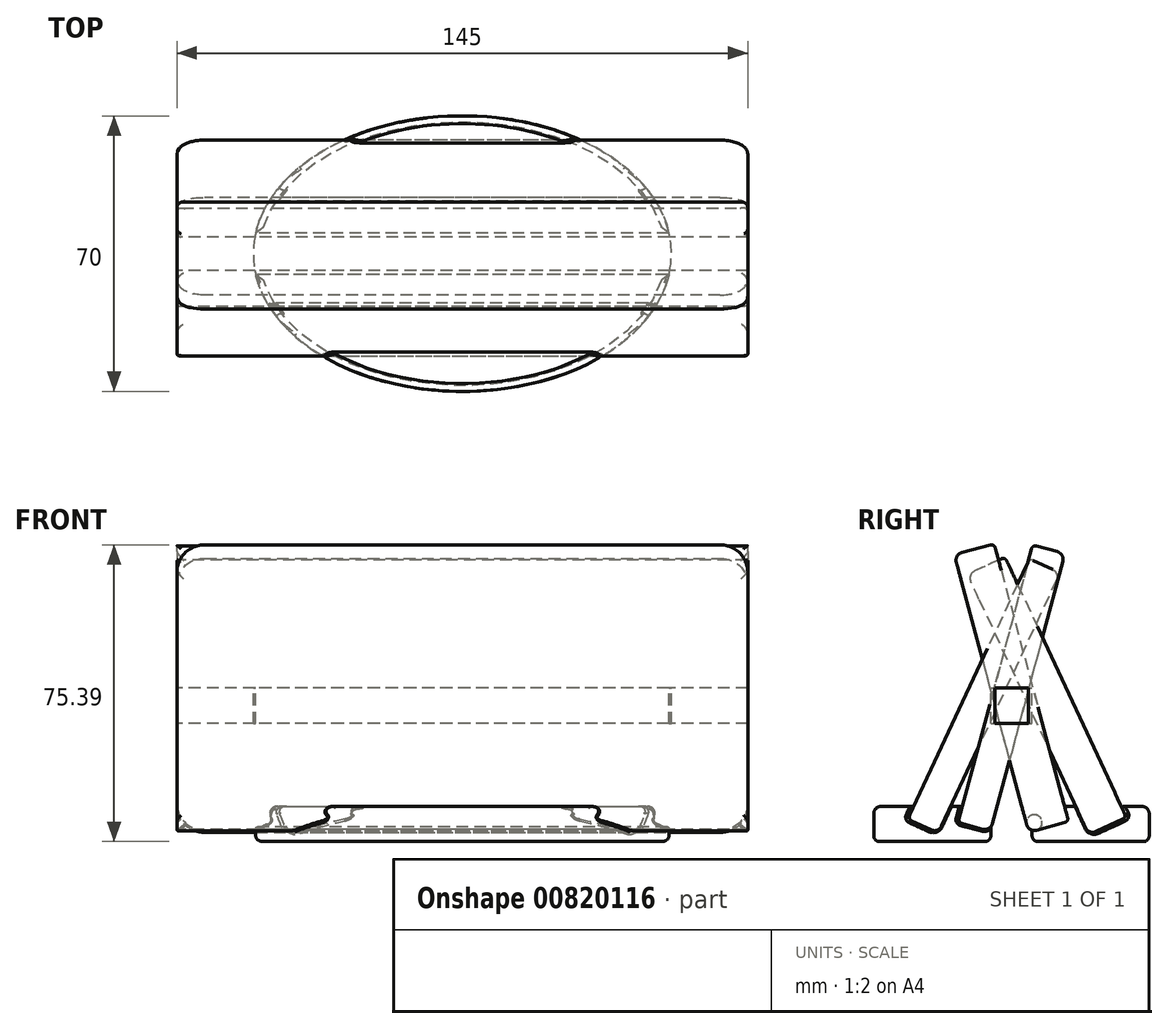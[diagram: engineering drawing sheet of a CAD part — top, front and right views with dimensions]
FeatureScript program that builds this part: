
annotation { "Feature Type Name" : "Feature", "Feature Type Description" : "" }
export const myFeature = defineFeature(function(context is Context, id is Id, definition is map)
    precondition{}
    {
        {
            var Q0;
            Q0=qCreatedBy(makeId("Top.planeOp"),FACE);
            var sketch = newSketch(context, id + "F0", { "sketchPlane" : qUnion([Q0])});
            skLineSegment(sketch, "E0.bottom", {"start": v(72.5, 5.25) * mm, "end": v(-72.5, 5.25) * mm});
            skLineSegment(sketch, "E0.top", {"start": v(72.5, -5.25) * mm, "end": v(-72.5, -5.25) * mm});
            skLineSegment(sketch, "E0.left", {"start": v(72.5, 5.25) * mm, "end": v(72.5, -5.25) * mm});
            skLineSegment(sketch, "E0.right", {"start": v(-72.5, 5.25) * mm, "end": v(-72.5, -5.25) * mm});
            skPoint(sketch, "E0.middle", {"position": v(0, 0) * mm});
            skLineSegment(sketch, "E1", {"start": v(-72.5, 0) * mm, "end": v(72.5, 0) * mm, "construction": true});
            skLineSegment(sketch, "E2", {"start": v(52.5, 5.25) * mm, "end": v(52.5, -5.25) * mm, "construction": true});
            skLineSegment(sketch, "E3", {"start": v(0, 0) * mm, "end": v(0, 35) * mm, "construction": true});
            skEllipse(sketch, "E4", {"center": v(0, 0) * mm, "majorRadius": 53.1 * mm, "minorRadius": 35 * mm, "majorAxis": v(1, 0)});
            skLineSegment(sketch, "E5", {"start": v(0, 35) * mm, "end": v(0, 40) * mm, "construction": true});
            skFitSpline(sketch, "E6.0", {"points": [v(58.05, -2.11) * mm, v(58.13, 0) * mm, v(58.05, 2.11) * mm, v(57.73, 4.9) * mm, v(56.95, 8.34) * mm, v(55.44, 12.3) * mm, v(53.38, 16.09) * mm, v(50.8, 19.67) * mm, v(47.77, 23.01) * mm, v(44.86, 25.6) * mm, v(42.32, 27.54) * mm, v(40.31, 28.94) * mm, v(38.21, 30.25) * mm, v(35.32, 31.9) * mm, v(31.51, 33.75) * mm, v(26.7, 35.65) * mm, v(21.67, 37.22) * mm, v(16.45, 38.45) * mm, v(11.08, 39.34) * mm, v(6.5, 39.79) * mm, v(2.8, 39.97) * mm, v(0, 40.02) * mm, v(-2.8, 39.97) * mm, v(-6.5, 39.79) * mm, v(-11.08, 39.34) * mm, v(-16.45, 38.45) * mm, v(-21.67, 37.22) * mm, v(-26.7, 35.65) * mm, v(-31.51, 33.75) * mm, v(-35.32, 31.9) * mm, v(-38.21, 30.25) * mm, v(-40.31, 28.94) * mm, v(-42.32, 27.54) * mm, v(-44.86, 25.6) * mm, v(-47.77, 23.01) * mm, v(-50.8, 19.67) * mm, v(-53.38, 16.09) * mm, v(-55.44, 12.3) * mm, v(-56.95, 8.34) * mm, v(-57.73, 4.9) * mm, v(-58.05, 2.11) * mm, v(-58.13, 0) * mm, v(-58.05, -2.11) * mm, v(-57.73, -4.9) * mm, v(-56.95, -8.34) * mm, v(-55.44, -12.3) * mm, v(-53.38, -16.09) * mm, v(-50.8, -19.67) * mm, v(-47.77, -23.01) * mm, v(-44.86, -25.6) * mm, v(-42.32, -27.54) * mm, v(-40.31, -28.94) * mm, v(-38.21, -30.25) * mm, v(-35.32, -31.9) * mm, v(-31.51, -33.75) * mm, v(-26.7, -35.65) * mm, v(-21.67, -37.22) * mm, v(-16.45, -38.45) * mm, v(-11.08, -39.34) * mm, v(-6.5, -39.79) * mm, v(-2.8, -39.97) * mm, v(0, -40.02) * mm, v(2.8, -39.97) * mm, v(6.5, -39.79) * mm, v(11.08, -39.34) * mm, v(16.45, -38.45) * mm, v(21.67, -37.22) * mm, v(26.7, -35.65) * mm, v(31.51, -33.75) * mm, v(35.32, -31.9) * mm, v(38.21, -30.25) * mm, v(40.31, -28.94) * mm, v(42.32, -27.54) * mm, v(44.86, -25.6) * mm, v(47.77, -23.01) * mm, v(50.8, -19.67) * mm, v(53.38, -16.09) * mm, v(55.44, -12.3) * mm, v(56.95, -8.34) * mm, v(57.73, -4.9) * mm, v(58.05, -2.11) * mm, v(58.13, 0) * mm, v(58.05, 2.11) * mm, v(58.05, -2.11) * mm]});
            skLineSegment(sketch, "E7.bottom", {"start": v(72.5, -4.25) * mm, "end": v(-72.5, -4.25) * mm});
            skLineSegment(sketch, "E7.top", {"start": v(72.5, 4.25) * mm, "end": v(-72.5, 4.25) * mm});
            skLineSegment(sketch, "E7.left", {"start": v(72.5, -4.25) * mm, "end": v(72.5, 4.25) * mm});
            skLineSegment(sketch, "E7.right", {"start": v(-72.5, -4.25) * mm, "end": v(-72.5, 4.25) * mm});
            skSolve(sketch);
        }
        {
            var Q0;
            {var subQ5=sQuery(id+"F0.wireOp",EDGE,"E7.right");Q0=makeQuery(id+"F0.imprint","IMPRINT",FACE,{"disambiguationData":[TD([[makeQuery(id+"F0.imprint","IMPRINT",EDGE,{"derivedFrom":subQ5}),-1.0]])]});}
            var Q1;
            {var subQ0=sQuery(id+"F0.wireOp",EDGE,"E7.top");var subQ1=sQuery(id+"F0.wireOp",EDGE,"E4");var subQ2=makeQuery(id+"F0.imprint","INTERSECT",VERTEX,{"disambiguationData":[OD(1.0)],"derivedFrom":[subQ1,subQ0]});Q1=makeQuery(id+"F0.imprint","IMPRINT",FACE,{"disambiguationData":[TD([[makeQuery(id+"F0.imprint","IMPRINT",EDGE,{"disambiguationData":[TD([[subQ2,-1.0]])],"derivedFrom":subQ1}),-1.0]])]});}
            var Q2;
            {var subQ0=sQuery(id+"F0.wireOp",EDGE,"E7.top");var subQ1=sQuery(id+"F0.wireOp",EDGE,"E4");var subQ2=makeQuery(id+"F0.imprint","INTERSECT",VERTEX,{"disambiguationData":[OD(1.0)],"derivedFrom":[subQ1,subQ0]});Q2=makeQuery(id+"F0.imprint","IMPRINT",FACE,{"disambiguationData":[TD([[makeQuery(id+"F0.imprint","IMPRINT",EDGE,{"disambiguationData":[TD([[subQ2,-1.0]])],"derivedFrom":subQ1}),1.0]])]});}
            var Q3;
            {var subQ0=sQuery(id+"F0.wireOp",EDGE,"E7.top");var subQ1=sQuery(id+"F0.wireOp",EDGE,"E4");var subQ2=makeQuery(id+"F0.imprint","INTERSECT",VERTEX,{"disambiguationData":[OD(0.0)],"derivedFrom":[subQ1,subQ0]});Q3=makeQuery(id+"F0.imprint","IMPRINT",FACE,{"disambiguationData":[TD([[makeQuery(id+"F0.imprint","IMPRINT",EDGE,{"disambiguationData":[TD([[subQ2,1.0]])],"derivedFrom":subQ1}),-1.0]])]});}
            var Q4;
            {var subQ5=sQuery(id+"F0.wireOp",EDGE,"E7.left");Q4=makeQuery(id+"F0.imprint","IMPRINT",FACE,{"disambiguationData":[TD([[makeQuery(id+"F0.imprint","IMPRINT",EDGE,{"derivedFrom":subQ5}),1.0]])]});}
            extrude(context, id + "F1", {"entities" : qUnion([Q0, Q1, Q2, Q3, Q4]), "depth" : 73 * mm, "offsetDistance" : 25 * mm, "symmetric" : true});
        }
        {
            var Q0;
            {var subQ5=sQuery(id+"F0.wireOp",EDGE,"E7.left");Q0=makeQuery(id+"F0.imprint","IMPRINT",FACE,{"disambiguationData":[TD([[makeQuery(id+"F0.imprint","IMPRINT",EDGE,{"derivedFrom":subQ5}),1.0]])]});}
            var Q1;
            {var subQ0=sQuery(id+"F0.wireOp",EDGE,"E0.left");var subQ1=sQuery(id+"F0.wireOp",EDGE,"E0.bottom");var subQ2=makeQuery(id+"F0.imprint","INTERSECT",VERTEX,{"derivedFrom":[subQ1,subQ0]});Q1=makeQuery(id+"F0.imprint","IMPRINT",FACE,{"disambiguationData":[TD([[makeQuery(id+"F0.imprint","IMPRINT",EDGE,{"disambiguationData":[TD([[subQ2,-1.0]])],"derivedFrom":subQ1}),1.0]])]});}
            var Q2;
            {var subQ0=sQuery(id+"F0.wireOp",EDGE,"E0.left");var subQ1=sQuery(id+"F0.wireOp",EDGE,"E0.top");var subQ2=makeQuery(id+"F0.imprint","INTERSECT",VERTEX,{"derivedFrom":[subQ1,subQ0]});Q2=makeQuery(id+"F0.imprint","IMPRINT",FACE,{"disambiguationData":[TD([[makeQuery(id+"F0.imprint","IMPRINT",EDGE,{"disambiguationData":[TD([[subQ2,-1.0]])],"derivedFrom":subQ1}),-1.0]])]});}
            var Q3;
            {var subQ0=sQuery(id+"F0.wireOp",EDGE,"E7.top");var subQ1=sQuery(id+"F0.wireOp",EDGE,"E4");var subQ2=makeQuery(id+"F0.imprint","INTERSECT",VERTEX,{"disambiguationData":[OD(0.0)],"derivedFrom":[subQ1,subQ0]});Q3=makeQuery(id+"F0.imprint","IMPRINT",FACE,{"disambiguationData":[TD([[makeQuery(id+"F0.imprint","IMPRINT",EDGE,{"disambiguationData":[TD([[subQ2,1.0]])],"derivedFrom":subQ1}),-1.0]])]});}
            var Q4;
            {var subQ0=sQuery(id+"F0.wireOp",EDGE,"E6.0");var subQ1=sQuery(id+"F0.wireOp",EDGE,"E0.bottom");var subQ2=makeQuery(id+"F0.imprint","INTERSECT",VERTEX,{"disambiguationData":[OD(0.0)],"derivedFrom":[subQ1,subQ0]});Q4=makeQuery(id+"F0.imprint","IMPRINT",FACE,{"disambiguationData":[TD([[makeQuery(id+"F0.imprint","IMPRINT",EDGE,{"disambiguationData":[TD([[subQ2,-1.0]])],"derivedFrom":subQ1}),1.0]])]});}
            var Q5;
            {var subQ0=sQuery(id+"F0.wireOp",EDGE,"E6.0");var subQ1=sQuery(id+"F0.wireOp",EDGE,"E0.top");var subQ2=makeQuery(id+"F0.imprint","INTERSECT",VERTEX,{"disambiguationData":[OD(0.0)],"derivedFrom":[subQ1,subQ0]});Q5=makeQuery(id+"F0.imprint","IMPRINT",FACE,{"disambiguationData":[TD([[makeQuery(id+"F0.imprint","IMPRINT",EDGE,{"disambiguationData":[TD([[subQ2,-1.0]])],"derivedFrom":subQ1}),-1.0]])]});}
            var Q6;
            {var subQ0=sQuery(id+"F0.wireOp",EDGE,"E7.top");var subQ1=sQuery(id+"F0.wireOp",EDGE,"E4");var subQ2=makeQuery(id+"F0.imprint","INTERSECT",VERTEX,{"disambiguationData":[OD(1.0)],"derivedFrom":[subQ1,subQ0]});Q6=makeQuery(id+"F0.imprint","IMPRINT",FACE,{"disambiguationData":[TD([[makeQuery(id+"F0.imprint","IMPRINT",EDGE,{"disambiguationData":[TD([[subQ2,-1.0]])],"derivedFrom":subQ1}),1.0]])]});}
            var Q7;
            {var subQ0=sQuery(id+"F0.wireOp",EDGE,"E4");var subQ1=sQuery(id+"F0.wireOp",EDGE,"E0.bottom");var subQ2=makeQuery(id+"F0.imprint","INTERSECT",VERTEX,{"disambiguationData":[OD(0.0)],"derivedFrom":[subQ1,subQ0]});Q7=makeQuery(id+"F0.imprint","IMPRINT",FACE,{"disambiguationData":[TD([[makeQuery(id+"F0.imprint","IMPRINT",EDGE,{"disambiguationData":[TD([[subQ2,-1.0]])],"derivedFrom":subQ1}),1.0]])]});}
            var Q8;
            {var subQ0=sQuery(id+"F0.wireOp",EDGE,"E4");var subQ1=sQuery(id+"F0.wireOp",EDGE,"E0.top");var subQ2=makeQuery(id+"F0.imprint","INTERSECT",VERTEX,{"disambiguationData":[OD(0.0)],"derivedFrom":[subQ1,subQ0]});Q8=makeQuery(id+"F0.imprint","IMPRINT",FACE,{"disambiguationData":[TD([[makeQuery(id+"F0.imprint","IMPRINT",EDGE,{"disambiguationData":[TD([[subQ2,-1.0]])],"derivedFrom":subQ1}),-1.0]])]});}
            var Q9;
            {var subQ0=sQuery(id+"F0.wireOp",EDGE,"E6.0");var subQ1=sQuery(id+"F0.wireOp",EDGE,"E0.bottom");var subQ2=makeQuery(id+"F0.imprint","INTERSECT",VERTEX,{"disambiguationData":[OD(1.0)],"derivedFrom":[subQ1,subQ0]});Q9=makeQuery(id+"F0.imprint","IMPRINT",FACE,{"disambiguationData":[TD([[makeQuery(id+"F0.imprint","IMPRINT",EDGE,{"disambiguationData":[TD([[subQ2,1.0]])],"derivedFrom":subQ1}),1.0]])]});}
            var Q10;
            {var subQ0=sQuery(id+"F0.wireOp",EDGE,"E7.top");var subQ1=sQuery(id+"F0.wireOp",EDGE,"E4");var subQ2=makeQuery(id+"F0.imprint","INTERSECT",VERTEX,{"disambiguationData":[OD(1.0)],"derivedFrom":[subQ1,subQ0]});Q10=makeQuery(id+"F0.imprint","IMPRINT",FACE,{"disambiguationData":[TD([[makeQuery(id+"F0.imprint","IMPRINT",EDGE,{"disambiguationData":[TD([[subQ2,-1.0]])],"derivedFrom":subQ1}),-1.0]])]});}
            var Q11;
            {var subQ0=sQuery(id+"F0.wireOp",EDGE,"E6.0");var subQ1=sQuery(id+"F0.wireOp",EDGE,"E0.top");var subQ2=makeQuery(id+"F0.imprint","INTERSECT",VERTEX,{"disambiguationData":[OD(1.0)],"derivedFrom":[subQ1,subQ0]});Q11=makeQuery(id+"F0.imprint","IMPRINT",FACE,{"disambiguationData":[TD([[makeQuery(id+"F0.imprint","IMPRINT",EDGE,{"disambiguationData":[TD([[subQ2,1.0]])],"derivedFrom":subQ1}),-1.0]])]});}
            var Q12;
            {var subQ0=sQuery(id+"F0.wireOp",EDGE,"E0.right");var subQ1=sQuery(id+"F0.wireOp",EDGE,"E0.bottom");var subQ2=makeQuery(id+"F0.imprint","INTERSECT",VERTEX,{"derivedFrom":[subQ1,subQ0]});Q12=makeQuery(id+"F0.imprint","IMPRINT",FACE,{"disambiguationData":[TD([[makeQuery(id+"F0.imprint","IMPRINT",EDGE,{"disambiguationData":[TD([[subQ2,1.0]])],"derivedFrom":subQ1}),1.0]])]});}
            var Q13;
            {var subQ5=sQuery(id+"F0.wireOp",EDGE,"E7.right");Q13=makeQuery(id+"F0.imprint","IMPRINT",FACE,{"disambiguationData":[TD([[makeQuery(id+"F0.imprint","IMPRINT",EDGE,{"derivedFrom":subQ5}),-1.0]])]});}
            var Q14;
            {var subQ0=sQuery(id+"F0.wireOp",EDGE,"E0.right");var subQ1=sQuery(id+"F0.wireOp",EDGE,"E0.top");var subQ2=makeQuery(id+"F0.imprint","INTERSECT",VERTEX,{"derivedFrom":[subQ1,subQ0]});Q14=makeQuery(id+"F0.imprint","IMPRINT",FACE,{"disambiguationData":[TD([[makeQuery(id+"F0.imprint","IMPRINT",EDGE,{"disambiguationData":[TD([[subQ2,1.0]])],"derivedFrom":subQ1}),-1.0]])]});}
            extrude(context, id + "F2", {"entities" : qUnion([Q0, Q1, Q2, Q3, Q4, Q5, Q6, Q7, Q8, Q9, Q10, Q11, Q12, Q13, Q14]), "depth" : 73 * mm, "offsetDistance" : 25 * mm, "symmetric" : true});
        }
        {
            var Q0;
            Q0=makeQuery(id+"F1.opExtrude","CAP_EDGE",EDGE,{"disambiguationData":[OSD([sQuery(id+"F0.wireOp",EDGE,"E7.left")])],"isStart":false});
            var Q1;
            Q1=makeQuery(id+"F1.opExtrude","CAP_EDGE",EDGE,{"disambiguationData":[OSD([sQuery(id+"F0.wireOp",EDGE,"E7.right")])],"isStart":false});
            var Q2;
            Q2=makeQuery(id+"F1.opExtrude","CAP_EDGE",EDGE,{"disambiguationData":[OSD([sQuery(id+"F0.wireOp",EDGE,"E7.left")])],"isStart":true});
            var Q3;
            Q3=makeQuery(id+"F1.opExtrude","CAP_EDGE",EDGE,{"disambiguationData":[OSD([sQuery(id+"F0.wireOp",EDGE,"E7.right")])],"isStart":true});
            var Q4;
            Q4=makeQuery(id+"F2.opExtrude","CAP_EDGE",EDGE,{"disambiguationData":[OSD([sQuery(id+"F0.wireOp",EDGE,"E0.right"),sQuery(id+"F0.wireOp",EDGE,"E7.right")])],"isStart":false});
            var Q5;
            Q5=makeQuery(id+"F2.opExtrude","CAP_EDGE",EDGE,{"disambiguationData":[OSD([sQuery(id+"F0.wireOp",EDGE,"E0.right"),sQuery(id+"F0.wireOp",EDGE,"E7.right")])],"isStart":true});
            var Q6;
            Q6=makeQuery(id+"F2.opExtrude","CAP_EDGE",EDGE,{"disambiguationData":[OSD([sQuery(id+"F0.wireOp",EDGE,"E0.left"),sQuery(id+"F0.wireOp",EDGE,"E7.left")])],"isStart":false});
            var Q7;
            Q7=makeQuery(id+"F2.opExtrude","CAP_EDGE",EDGE,{"disambiguationData":[OSD([sQuery(id+"F0.wireOp",EDGE,"E0.left"),sQuery(id+"F0.wireOp",EDGE,"E7.left")])],"isStart":true});
            fillet(context, id + "F3", {"entities" : qUnion([Q0, Q1, Q2, Q3, Q4, Q5, Q6, Q7]), "radius" : 7 * mm, "tangentPropagation" : true, "allowEdgeOverflow" : false});
        }
        {
            var Q0;
            Q0=makeQuery(id+"F1.opExtrude","SWEPT_BODY",BODY,{"disambiguationData":[OSD([sQuery(id+"F0.wireOp",EDGE,"E7.bottom"),sQuery(id+"F0.wireOp",EDGE,"E7.top"),sQuery(id+"F0.wireOp",EDGE,"E7.left"),sQuery(id+"F0.wireOp",EDGE,"E7.right")])]});
            transform(context, id + "F4", {"entities" : qUnion([Q0]), "transformType" : TransformType.TRANSLATION_3D, "dx" : 0 * mm, "dy" : 0 * mm, "dz" : 0 * mm, "makeCopy" : true});
        }
        {
            var Q0;
            Q0=makeQuery(id+"F2.opExtrude","SWEPT_BODY",BODY,{"disambiguationData":[OSD([sQuery(id+"F0.wireOp",EDGE,"E0.bottom"),sQuery(id+"F0.wireOp",EDGE,"E0.top"),sQuery(id+"F0.wireOp",EDGE,"E0.left"),sQuery(id+"F0.wireOp",EDGE,"E0.right"),sQuery(id+"F0.wireOp",EDGE,"E7.left"),sQuery(id+"F0.wireOp",EDGE,"E7.right")])]});
            transform(context, id + "F5", {"entities" : qUnion([Q0]), "transformType" : TransformType.TRANSLATION_3D, "dx" : 0 * mm, "dy" : 0 * mm, "dz" : 0 * mm, "makeCopy" : true});
        }
        {
            var Q0;
            Q0=makeQuery(id+"F4.opPattern","COPY",BODY,{"derivedFrom":makeQuery(id+"F1.opExtrude","SWEPT_BODY",BODY,{"disambiguationData":[OSD([sQuery(id+"F0.wireOp",EDGE,"E7.bottom"),sQuery(id+"F0.wireOp",EDGE,"E7.top"),sQuery(id+"F0.wireOp",EDGE,"E7.left"),sQuery(id+"F0.wireOp",EDGE,"E7.right")])]}),"instanceName":"1"});
            var Q1;
            Q1=sQuery(id+"F0.wireOp",EDGE,"E1");
            transform(context, id + "F6", {"entities" : qUnion([Q0]), "transformType" : TransformType.ROTATION, "transformAxis" : qUnion([Q1]), "angle" : 15 * degree, "oppositeDirection" : true, "makeCopy" : false});
        }
        {
            var Q0;
            Q0=makeQuery(id+"F5.opPattern","COPY",BODY,{"derivedFrom":makeQuery(id+"F2.opExtrude","SWEPT_BODY",BODY,{"disambiguationData":[OSD([sQuery(id+"F0.wireOp",EDGE,"E0.bottom"),sQuery(id+"F0.wireOp",EDGE,"E0.top"),sQuery(id+"F0.wireOp",EDGE,"E0.left"),sQuery(id+"F0.wireOp",EDGE,"E0.right"),sQuery(id+"F0.wireOp",EDGE,"E7.left"),sQuery(id+"F0.wireOp",EDGE,"E7.right")])]}),"instanceName":"1"});
            var Q1;
            Q1=sQuery(id+"F0.wireOp",EDGE,"E1");
            transform(context, id + "F7", {"entities" : qUnion([Q0]), "transformType" : TransformType.ROTATION, "transformAxis" : qUnion([Q1]), "angle" : 15 * degree, "makeCopy" : false});
        }
        {
            var Q0;
            Q0=makeQuery(id+"F1.opExtrude","SWEPT_BODY",BODY,{"disambiguationData":[OSD([sQuery(id+"F0.wireOp",EDGE,"E7.bottom"),sQuery(id+"F0.wireOp",EDGE,"E7.top"),sQuery(id+"F0.wireOp",EDGE,"E7.left"),sQuery(id+"F0.wireOp",EDGE,"E7.right")])]});
            var Q1;
            Q1=sQuery(id+"F0.wireOp",EDGE,"E1");
            transform(context, id + "F8", {"entities" : qUnion([Q0]), "transformType" : TransformType.ROTATION, "transformAxis" : qUnion([Q1]), "angle" : 25 * degree, "oppositeDirection" : true, "makeCopy" : false});
        }
        {
            var Q0;
            Q0=makeQuery(id+"F2.opExtrude","SWEPT_BODY",BODY,{"disambiguationData":[OSD([sQuery(id+"F0.wireOp",EDGE,"E0.bottom"),sQuery(id+"F0.wireOp",EDGE,"E0.top"),sQuery(id+"F0.wireOp",EDGE,"E0.left"),sQuery(id+"F0.wireOp",EDGE,"E0.right"),sQuery(id+"F0.wireOp",EDGE,"E7.left"),sQuery(id+"F0.wireOp",EDGE,"E7.right")])]});
            var Q1;
            Q1=sQuery(id+"F0.wireOp",EDGE,"E1");
            transform(context, id + "F9", {"entities" : qUnion([Q0]), "transformType" : TransformType.ROTATION, "transformAxis" : qUnion([Q1]), "angle" : 25 * degree, "makeCopy" : false});
        }
        {
            var Q0;
            Q0=makeQuery(id+"F1.opExtrude","SWEPT_BODY",BODY,{"disambiguationData":[OSD([sQuery(id+"F0.wireOp",EDGE,"E7.bottom"),sQuery(id+"F0.wireOp",EDGE,"E7.top"),sQuery(id+"F0.wireOp",EDGE,"E7.left"),sQuery(id+"F0.wireOp",EDGE,"E7.right")])]});
            transform(context, id + "F10", {"entities" : qUnion([Q0]), "transformType" : TransformType.TRANSLATION_3D, "dx" : 0 * mm, "dy" : -7 * mm, "dz" : -2 * mm, "makeCopy" : false});
        }
        {
            var Q0;
            Q0=makeQuery(id+"F2.opExtrude","SWEPT_BODY",BODY,{"disambiguationData":[OSD([sQuery(id+"F0.wireOp",EDGE,"E0.bottom"),sQuery(id+"F0.wireOp",EDGE,"E0.top"),sQuery(id+"F0.wireOp",EDGE,"E0.left"),sQuery(id+"F0.wireOp",EDGE,"E0.right"),sQuery(id+"F0.wireOp",EDGE,"E7.left"),sQuery(id+"F0.wireOp",EDGE,"E7.right")])]});
            transform(context, id + "F11", {"entities" : qUnion([Q0]), "transformType" : TransformType.TRANSLATION_3D, "dx" : 0 * mm, "dy" : 9 * mm, "dz" : -2 * mm, "makeCopy" : false});
        }
        {
            var Q0;
            Q0=makeQuery(id+"F2.opExtrude","SWEPT_FACE",FACE,{"disambiguationData":[OSD([sQuery(id+"F0.wireOp",EDGE,"E0.bottom")])]});
            var Q1;
            Q1=makeQuery(id+"F5.opPattern","COPY",FACE,{"derivedFrom":makeQuery(id+"F2.opExtrude","SWEPT_FACE",FACE,{"disambiguationData":[OSD([sQuery(id+"F0.wireOp",EDGE,"E0.bottom")])]}),"instanceName":"1"});
            var Q2;
            Q2=makeQuery(id+"F4.opPattern","COPY",FACE,{"derivedFrom":makeQuery(id+"F1.opExtrude","SWEPT_FACE",FACE,{"disambiguationData":[OSD([sQuery(id+"F0.wireOp",EDGE,"E7.bottom")])]}),"instanceName":"1"});
            var Q3;
            Q3=makeQuery(id+"F1.opExtrude","SWEPT_FACE",FACE,{"disambiguationData":[OSD([sQuery(id+"F0.wireOp",EDGE,"E7.bottom")])]});
            fillet(context, id + "F12", {"entities" : qUnion([Q0, Q1, Q2, Q3]), "radius" : 1 * mm, "tangentPropagation" : true, "allowEdgeOverflow" : false});
        }
        {
            var Q0;
            Q0=makeQuery(id+"F1.opExtrude","SWEPT_FACE",FACE,{"disambiguationData":[OSD([sQuery(id+"F0.wireOp",EDGE,"E7.top")])]});
            var Q1;
            Q1=makeQuery(id+"F4.opPattern","COPY",FACE,{"derivedFrom":makeQuery(id+"F1.opExtrude","SWEPT_FACE",FACE,{"disambiguationData":[OSD([sQuery(id+"F0.wireOp",EDGE,"E7.top")])]}),"instanceName":"1"});
            var Q2;
            Q2=makeQuery(id+"F5.opPattern","COPY",FACE,{"derivedFrom":makeQuery(id+"F2.opExtrude","SWEPT_FACE",FACE,{"disambiguationData":[OSD([sQuery(id+"F0.wireOp",EDGE,"E0.top")])]}),"instanceName":"1"});
            var Q3;
            Q3=makeQuery(id+"F2.opExtrude","SWEPT_FACE",FACE,{"disambiguationData":[OSD([sQuery(id+"F0.wireOp",EDGE,"E0.top")])]});
            fillet(context, id + "F13", {"entities" : qUnion([Q0, Q1, Q2, Q3]), "radius" : 2 * mm, "tangentPropagation" : true, "allowEdgeOverflow" : false});
        }
        {
            var Q0;
            {var subQ0=sQuery(id+"F0.wireOp",EDGE,"E6.0");var subQ1=sQuery(id+"F0.wireOp",EDGE,"E0.bottom");var subQ2=makeQuery(id+"F0.imprint","INTERSECT",VERTEX,{"disambiguationData":[OD(0.0)],"derivedFrom":[subQ1,subQ0]});Q0=makeQuery(id+"F0.imprint","IMPRINT",FACE,{"disambiguationData":[TD([[makeQuery(id+"F0.imprint","IMPRINT",EDGE,{"disambiguationData":[TD([[subQ2,-1.0]])],"derivedFrom":subQ1}),-1.0]])]});}
            var Q1;
            {var subQ0=sQuery(id+"F0.wireOp",EDGE,"E6.0");var subQ1=sQuery(id+"F0.wireOp",EDGE,"E0.bottom");var subQ2=makeQuery(id+"F0.imprint","INTERSECT",VERTEX,{"disambiguationData":[OD(0.0)],"derivedFrom":[subQ1,subQ0]});Q1=makeQuery(id+"F0.imprint","IMPRINT",FACE,{"disambiguationData":[TD([[makeQuery(id+"F0.imprint","IMPRINT",EDGE,{"disambiguationData":[TD([[subQ2,-1.0]])],"derivedFrom":subQ1}),1.0]])]});}
            var Q2;
            {var subQ0=sQuery(id+"F0.wireOp",EDGE,"E7.top");var subQ1=sQuery(id+"F0.wireOp",EDGE,"E4");var subQ2=makeQuery(id+"F0.imprint","INTERSECT",VERTEX,{"disambiguationData":[OD(0.0)],"derivedFrom":[subQ1,subQ0]});Q2=makeQuery(id+"F0.imprint","IMPRINT",FACE,{"disambiguationData":[TD([[makeQuery(id+"F0.imprint","IMPRINT",EDGE,{"disambiguationData":[TD([[subQ2,1.0]])],"derivedFrom":subQ1}),-1.0]])]});}
            var Q3;
            {var subQ0=sQuery(id+"F0.wireOp",EDGE,"E6.0");var subQ1=sQuery(id+"F0.wireOp",EDGE,"E0.top");var subQ2=makeQuery(id+"F0.imprint","INTERSECT",VERTEX,{"disambiguationData":[OD(0.0)],"derivedFrom":[subQ1,subQ0]});Q3=makeQuery(id+"F0.imprint","IMPRINT",FACE,{"disambiguationData":[TD([[makeQuery(id+"F0.imprint","IMPRINT",EDGE,{"disambiguationData":[TD([[subQ2,-1.0]])],"derivedFrom":subQ1}),-1.0]])]});}
            var Q4;
            {var subQ0=sQuery(id+"F0.wireOp",EDGE,"E6.0");var subQ1=sQuery(id+"F0.wireOp",EDGE,"E0.bottom");var subQ2=makeQuery(id+"F0.imprint","INTERSECT",VERTEX,{"disambiguationData":[OD(1.0)],"derivedFrom":[subQ1,subQ0]});Q4=makeQuery(id+"F0.imprint","IMPRINT",FACE,{"disambiguationData":[TD([[makeQuery(id+"F0.imprint","IMPRINT",EDGE,{"disambiguationData":[TD([[subQ2,1.0]])],"derivedFrom":subQ1}),1.0]])]});}
            var Q5;
            {var subQ0=sQuery(id+"F0.wireOp",EDGE,"E7.top");var subQ1=sQuery(id+"F0.wireOp",EDGE,"E4");var subQ2=makeQuery(id+"F0.imprint","INTERSECT",VERTEX,{"disambiguationData":[OD(1.0)],"derivedFrom":[subQ1,subQ0]});Q5=makeQuery(id+"F0.imprint","IMPRINT",FACE,{"disambiguationData":[TD([[makeQuery(id+"F0.imprint","IMPRINT",EDGE,{"disambiguationData":[TD([[subQ2,-1.0]])],"derivedFrom":subQ1}),-1.0]])]});}
            var Q6;
            {var subQ0=sQuery(id+"F0.wireOp",EDGE,"E6.0");var subQ1=sQuery(id+"F0.wireOp",EDGE,"E0.top");var subQ2=makeQuery(id+"F0.imprint","INTERSECT",VERTEX,{"disambiguationData":[OD(1.0)],"derivedFrom":[subQ1,subQ0]});Q6=makeQuery(id+"F0.imprint","IMPRINT",FACE,{"disambiguationData":[TD([[makeQuery(id+"F0.imprint","IMPRINT",EDGE,{"disambiguationData":[TD([[subQ2,1.0]])],"derivedFrom":subQ1}),-1.0]])]});}
            var Q7;
            {var subQ0=sQuery(id+"F0.wireOp",EDGE,"E6.0");var subQ1=sQuery(id+"F0.wireOp",EDGE,"E0.top");var subQ2=makeQuery(id+"F0.imprint","INTERSECT",VERTEX,{"disambiguationData":[OD(0.0)],"derivedFrom":[subQ1,subQ0]});Q7=makeQuery(id+"F0.imprint","IMPRINT",FACE,{"disambiguationData":[TD([[makeQuery(id+"F0.imprint","IMPRINT",EDGE,{"disambiguationData":[TD([[subQ2,-1.0]])],"derivedFrom":subQ1}),1.0]])]});}
            extrude(context, id + "F14", {"entities" : qUnion([Q0, Q1, Q2, Q3, Q4, Q5, Q6, Q7]), "oppositeDirection" : true, "depth" : 9 * mm, "offsetDistance" : 25 * mm});
        }
        {
            var Q0;
            Q0=makeQuery(id+"F14.opExtrude","SWEPT_BODY",BODY,{"disambiguationData":[OSD([sQuery(id+"F0.wireOp",EDGE,"E4"),sQuery(id+"F0.wireOp",EDGE,"E6.0")])]});
            transform(context, id + "F15", {"entities" : qUnion([Q0]), "transformType" : TransformType.TRANSLATION_3D, "dx" : 0 * mm, "dy" : 0 * mm, "dz" : -30 * mm, "makeCopy" : false});
        }
        {
            var Q0;
            Q0=makeQuery(id+"F14.opExtrude","CAP_FACE",FACE,{"disambiguationData":[OSD([sQuery(id+"F0.wireOp",EDGE,"E4"),sQuery(id+"F0.wireOp",EDGE,"E6.0")])],"isStart":true});
            fillet(context, id + "F16", {"entities" : qUnion([Q0]), "radius" : 2 * mm, "tangentPropagation" : true, "allowEdgeOverflow" : false});
        }
        {
            var Q0;
            Q0=makeQuery(id+"F1.opExtrude","SWEPT_BODY",BODY,{"disambiguationData":[OSD([sQuery(id+"F0.wireOp",EDGE,"E7.bottom"),sQuery(id+"F0.wireOp",EDGE,"E7.top"),sQuery(id+"F0.wireOp",EDGE,"E7.left"),sQuery(id+"F0.wireOp",EDGE,"E7.right")])]});
            var Q1;
            Q1=makeQuery(id+"F2.opExtrude","SWEPT_BODY",BODY,{"disambiguationData":[OSD([sQuery(id+"F0.wireOp",EDGE,"E0.bottom"),sQuery(id+"F0.wireOp",EDGE,"E0.top"),sQuery(id+"F0.wireOp",EDGE,"E0.left"),sQuery(id+"F0.wireOp",EDGE,"E0.right"),sQuery(id+"F0.wireOp",EDGE,"E7.left"),sQuery(id+"F0.wireOp",EDGE,"E7.right")])]});
            var Q2;
            Q2=makeQuery(id+"F4.opPattern","COPY",BODY,{"derivedFrom":makeQuery(id+"F1.opExtrude","SWEPT_BODY",BODY,{"disambiguationData":[OSD([sQuery(id+"F0.wireOp",EDGE,"E7.bottom"),sQuery(id+"F0.wireOp",EDGE,"E7.top"),sQuery(id+"F0.wireOp",EDGE,"E7.left"),sQuery(id+"F0.wireOp",EDGE,"E7.right")])]}),"instanceName":"1"});
            var Q3;
            Q3=makeQuery(id+"F5.opPattern","COPY",BODY,{"derivedFrom":makeQuery(id+"F2.opExtrude","SWEPT_BODY",BODY,{"disambiguationData":[OSD([sQuery(id+"F0.wireOp",EDGE,"E0.bottom"),sQuery(id+"F0.wireOp",EDGE,"E0.top"),sQuery(id+"F0.wireOp",EDGE,"E0.left"),sQuery(id+"F0.wireOp",EDGE,"E0.right"),sQuery(id+"F0.wireOp",EDGE,"E7.left"),sQuery(id+"F0.wireOp",EDGE,"E7.right")])]}),"instanceName":"1"});
            var Q4;
            Q4=makeQuery(id+"F14.opExtrude","SWEPT_BODY",BODY,{"disambiguationData":[OSD([sQuery(id+"F0.wireOp",EDGE,"E4"),sQuery(id+"F0.wireOp",EDGE,"E6.0")])]});
            booleanBodies(context, id + "F17", {"operationType" : BooleanOperationType.SUBTRACTION, "tools" : qUnion([Q0, Q1, Q2, Q3]), "targets" : qUnion([Q4]), "keepTools" : true});
        }
        {
            var Q0;
            Q0=makeQuery(id+"F14.opExtrude","CAP_FACE",FACE,{"disambiguationData":[OSD([sQuery(id+"F0.wireOp",EDGE,"E4"),sQuery(id+"F0.wireOp",EDGE,"E6.0")])],"isStart":false});
            fillet(context, id + "F18", {"entities" : qUnion([Q0]), "radius" : 1.5 * mm, "tangentPropagation" : true, "allowEdgeOverflow" : false});
        }
        {
            var Q0;
            Q0=makeQuery(id+"F17.opBoolean","INTERSECT",EDGE,{"disambiguationData":[OD(1.0)],"derivedFrom":[makeQuery(id+"F1.opExtrude","SWEPT_FACE",FACE,{"disambiguationData":[OSD([sQuery(id+"F0.wireOp",EDGE,"E7.bottom")])]}),makeQuery(id+"F16.opFillet","BLEND_FACE",FACE,{"disambiguationData":[OSD([sQuery(id+"F0.wireOp",EDGE,"E6.0")])]})]});
            var Q1;
            Q1=makeQuery(id+"F17.opBoolean","INTERSECT",EDGE,{"disambiguationData":[OD(1.0)],"derivedFrom":[makeQuery(id+"F4.opPattern","COPY",FACE,{"derivedFrom":makeQuery(id+"F1.opExtrude","SWEPT_FACE",FACE,{"disambiguationData":[OSD([sQuery(id+"F0.wireOp",EDGE,"E7.bottom")])]}),"instanceName":"1"}),makeQuery(id+"F16.opFillet","BLEND_FACE",FACE,{"disambiguationData":[OSD([sQuery(id+"F0.wireOp",EDGE,"E6.0")])]})]});
            var Q2;
            Q2=makeQuery(id+"F17.opBoolean","INTERSECT",EDGE,{"disambiguationData":[OD(1.0)],"derivedFrom":[makeQuery(id+"F5.opPattern","COPY",FACE,{"derivedFrom":makeQuery(id+"F2.opExtrude","SWEPT_FACE",FACE,{"disambiguationData":[OSD([sQuery(id+"F0.wireOp",EDGE,"E0.top")])]}),"instanceName":"1"}),makeQuery(id+"F14.opExtrude","SWEPT_FACE",FACE,{"disambiguationData":[OSD([sQuery(id+"F0.wireOp",EDGE,"E6.0")])]})]});
            var Q3;
            Q3=makeQuery(id+"F17.opBoolean","INTERSECT",EDGE,{"disambiguationData":[OD(1.0)],"derivedFrom":[makeQuery(id+"F2.opExtrude","SWEPT_FACE",FACE,{"disambiguationData":[OSD([sQuery(id+"F0.wireOp",EDGE,"E0.top")])]}),makeQuery(id+"F14.opExtrude","SWEPT_FACE",FACE,{"disambiguationData":[OSD([sQuery(id+"F0.wireOp",EDGE,"E6.0")])]})]});
            var Q4;
            Q4=makeQuery(id+"F17.opBoolean","INTERSECT",EDGE,{"disambiguationData":[OD(0.0)],"derivedFrom":[makeQuery(id+"F2.opExtrude","SWEPT_FACE",FACE,{"disambiguationData":[OSD([sQuery(id+"F0.wireOp",EDGE,"E0.top")])]}),makeQuery(id+"F14.opExtrude","SWEPT_FACE",FACE,{"disambiguationData":[OSD([sQuery(id+"F0.wireOp",EDGE,"E4")])]})]});
            var Q5;
            Q5=makeQuery(id+"F17.opBoolean","INTERSECT",EDGE,{"disambiguationData":[OD(0.0)],"derivedFrom":[makeQuery(id+"F5.opPattern","COPY",FACE,{"derivedFrom":makeQuery(id+"F2.opExtrude","SWEPT_FACE",FACE,{"disambiguationData":[OSD([sQuery(id+"F0.wireOp",EDGE,"E0.top")])]}),"instanceName":"1"}),makeQuery(id+"F14.opExtrude","SWEPT_FACE",FACE,{"disambiguationData":[OSD([sQuery(id+"F0.wireOp",EDGE,"E4")])]})]});
            var Q6;
            Q6=makeQuery(id+"F17.opBoolean","INTERSECT",EDGE,{"disambiguationData":[OD(0.0)],"derivedFrom":[makeQuery(id+"F4.opPattern","COPY",FACE,{"derivedFrom":makeQuery(id+"F1.opExtrude","SWEPT_FACE",FACE,{"disambiguationData":[OSD([sQuery(id+"F0.wireOp",EDGE,"E7.bottom")])]}),"instanceName":"1"}),makeQuery(id+"F16.opFillet","BLEND_FACE",FACE,{"disambiguationData":[OSD([sQuery(id+"F0.wireOp",EDGE,"E4")])]})]});
            var Q7;
            Q7=makeQuery(id+"F17.opBoolean","INTERSECT",EDGE,{"disambiguationData":[OD(0.0)],"derivedFrom":[makeQuery(id+"F1.opExtrude","CAP_FACE",FACE,{"disambiguationData":[OSD([sQuery(id+"F0.wireOp",EDGE,"E7.bottom"),sQuery(id+"F0.wireOp",EDGE,"E7.top"),sQuery(id+"F0.wireOp",EDGE,"E7.left"),sQuery(id+"F0.wireOp",EDGE,"E7.right")])],"isStart":true}),makeQuery(id+"F14.opExtrude","SWEPT_FACE",FACE,{"disambiguationData":[OSD([sQuery(id+"F0.wireOp",EDGE,"E4")])]})]});
            fillet(context, id + "F19", {"entities" : qUnion([Q0, Q1, Q2, Q3, Q4, Q5, Q6, Q7]), "tangentPropagation" : true, "radius" : 0.5 * mm, "defaultsChanged" : true, "vertexSettings" : [], "allowEdgeOverflow" : false});
        }
    });
